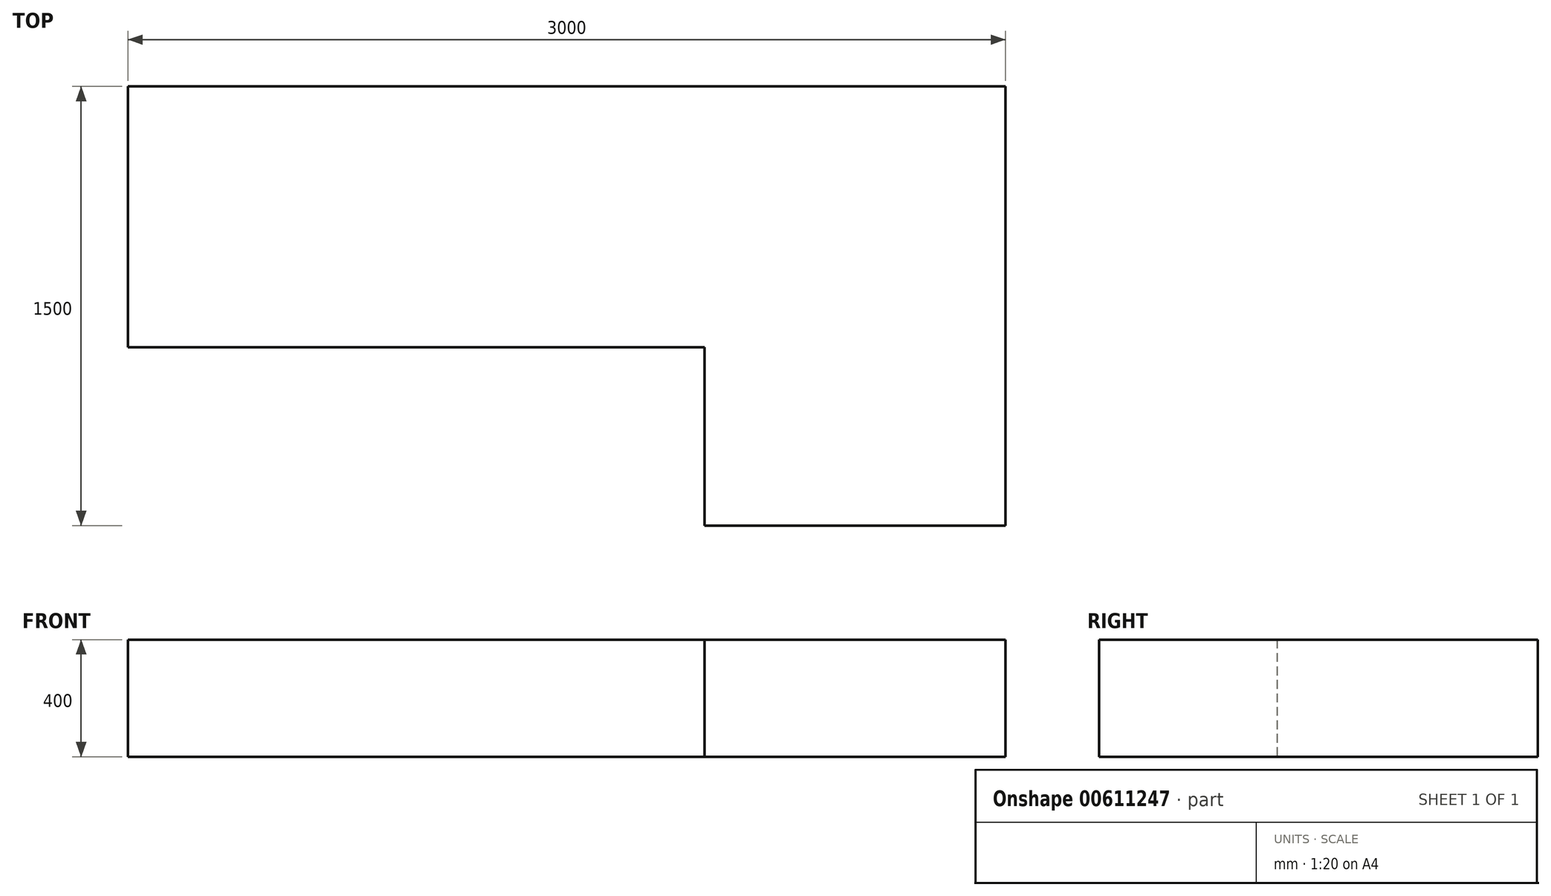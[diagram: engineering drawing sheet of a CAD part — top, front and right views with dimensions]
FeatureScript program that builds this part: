
annotation { "Feature Type Name" : "Feature", "Feature Type Description" : "" }
export const myFeature = defineFeature(function(context is Context, id is Id, definition is map)
    precondition{}
    {
        {
            var Q0;
            Q0=qCreatedBy(makeId("Top.planeOp"),FACE);
            var sketch = newSketch(context, id + "F0", { "sketchPlane" : qUnion([Q0])});
            skLineSegment(sketch, "E0", {"start": v(0, 0) * mm, "end": v(0, 891.57) * mm});
            skLineSegment(sketch, "E1", {"start": v(0, 891.57) * mm, "end": v(3000, 891.57) * mm});
            skLineSegment(sketch, "E2", {"start": v(3000, 891.57) * mm, "end": v(3000, -608.43) * mm});
            skLineSegment(sketch, "E3", {"start": v(3000, -608.43) * mm, "end": v(1970.75, -608.43) * mm});
            skLineSegment(sketch, "E4", {"start": v(1970.75, -608.43) * mm, "end": v(1970.75, 0) * mm});
            skLineSegment(sketch, "E5", {"start": v(1970.75, 0) * mm, "end": v(0, 0) * mm});
            skSolve(sketch);
        }
        {
            var Q0;
            Q0=makeQuery(id+"F0.imprint","IMPRINT",FACE,{"disambiguationData":[TD([[makeQuery(id+"F0.imprint","IMPRINT",EDGE,{"derivedFrom":sQuery(id+"F0.wireOp",EDGE,"E0")}),-1.0]])]});
            extrude(context, id + "F1", {"entities" : qUnion([Q0]), "depth" : 400 * mm, "offsetDistance" : 25 * mm});
        }
    });
